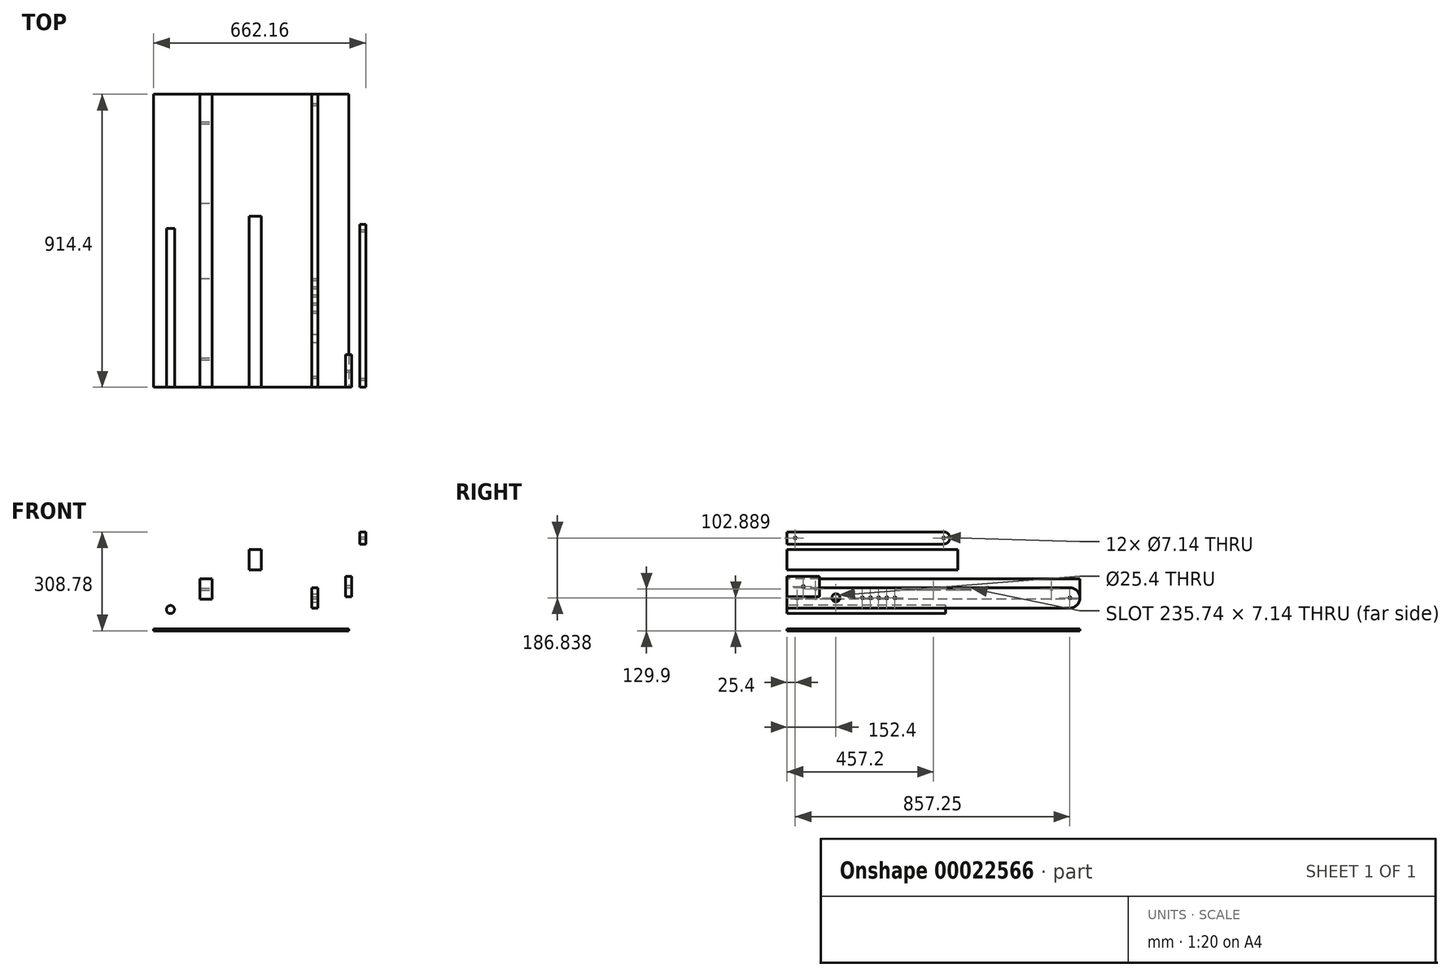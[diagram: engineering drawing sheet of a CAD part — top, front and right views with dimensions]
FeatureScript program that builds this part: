
annotation { "Feature Type Name" : "Feature", "Feature Type Description" : "" }
export const myFeature = defineFeature(function(context is Context, id is Id, definition is map)
    precondition{}
    {
        {
            var Q0;
            Q0=qCreatedBy(makeId("Front.planeOp"),FACE);
            var sketch = newSketch(context, id + "F0", { "sketchPlane" : qUnion([Q0])});
            skLineSegment(sketch, "E0.bottom", {"start": v(38.1, 63.5) * mm, "end": v(0, 63.5) * mm});
            skLineSegment(sketch, "E0.top", {"start": v(38.1, 0) * mm, "end": v(0, 0) * mm});
            skLineSegment(sketch, "E0.left", {"start": v(38.1, 63.5) * mm, "end": v(38.1, 0) * mm});
            skLineSegment(sketch, "E0.right", {"start": v(0, 63.5) * mm, "end": v(0, 0) * mm});
            skSolve(sketch);
        }
        {
            var Q0;
            Q0=qSketchRegion(id+"F0",true);
            extrude(context, id + "F1", {"entities" : qUnion([Q0]), "oppositeDirection" : true, "depth" : 914.4 * mm});
        }
        {
            var Q0;
            Q0=qCreatedBy(makeId("Front.planeOp"),FACE);
            var sketch = newSketch(context, id + "F2", { "sketchPlane" : qUnion([Q0])});
            skLineSegment(sketch, "E1.bottom", {"start": v(153.85, 91.9) * mm, "end": v(191.95, 91.9) * mm});
            skLineSegment(sketch, "E1.top", {"start": v(153.85, 155.4) * mm, "end": v(191.95, 155.4) * mm});
            skLineSegment(sketch, "E1.left", {"start": v(153.85, 91.9) * mm, "end": v(153.85, 155.4) * mm});
            skLineSegment(sketch, "E1.right", {"start": v(191.95, 91.9) * mm, "end": v(191.95, 155.4) * mm});
            skSolve(sketch);
        }
        {
            var Q0;
            Q0=makeQuery(id+"F2.imprint","IMPRINT",FACE,{"disambiguationData":[TD([[makeQuery(id+"F2.imprint","IMPRINT",EDGE,{"derivedFrom":sQuery(id+"F2.wireOp",EDGE,"E1.bottom")}),1.0]])]});
            extrude(context, id + "F3", {"entities" : qUnion([Q0]), "oppositeDirection" : true, "depth" : 533.4 * mm});
        }
        {
            var Q0;
            Q0=qCreatedBy(makeId("Front.planeOp"),FACE);
            var sketch = newSketch(context, id + "F4", { "sketchPlane" : qUnion([Q0])});
            skLineSegment(sketch, "E2.bottom", {"start": v(349.93, -27.01) * mm, "end": v(368.98, -27.01) * mm});
            skLineSegment(sketch, "E2.top", {"start": v(349.93, 36.49) * mm, "end": v(368.98, 36.49) * mm});
            skLineSegment(sketch, "E2.left", {"start": v(349.93, -27.01) * mm, "end": v(349.93, 36.49) * mm});
            skLineSegment(sketch, "E2.right", {"start": v(368.98, -27.01) * mm, "end": v(368.98, 36.49) * mm});
            skSolve(sketch);
        }
        {
            var Q0;
            Q0=qSketchRegion(id+"F4",true);
            extrude(context, id + "F5", {"entities" : qUnion([Q0]), "oppositeDirection" : true, "depth" : 914.4 * mm});
        }
        {
            var Q0;
            Q0=qCreatedBy(makeId("Front.planeOp"),FACE);
            var sketch = newSketch(context, id + "F6", { "sketchPlane" : qUnion([Q0])});
            skLineSegment(sketch, "E3.bottom", {"start": v(454.55, 8.02) * mm, "end": v(473.6, 8.02) * mm});
            skLineSegment(sketch, "E3.top", {"start": v(454.55, 71.52) * mm, "end": v(473.6, 71.52) * mm});
            skLineSegment(sketch, "E3.left", {"start": v(454.55, 8.02) * mm, "end": v(454.55, 71.52) * mm});
            skLineSegment(sketch, "E3.right", {"start": v(473.6, 8.02) * mm, "end": v(473.6, 71.52) * mm});
            skSolve(sketch);
        }
        {
            var Q0;
            Q0=qSketchRegion(id+"F6",true);
            extrude(context, id + "F7", {"entities" : qUnion([Q0]), "oppositeDirection" : true, "depth" : 101.6 * mm});
        }
        {
            var Q0;
            Q0=makeQuery(id+"F5.opExtrude","SWEPT_FACE",FACE,{"disambiguationData":[OSD([sQuery(id+"F4.wireOp",EDGE,"E2.right")])]});
            var sketch = newSketch(context, id + "F8", { "sketchPlane" : qUnion([Q0])});
            skArc(sketch, "E4", {"start": v(882.65, -27.01) * mm, "mid": v(914.4, 4.74) * mm, "end": v(882.65, 36.49) * mm});
            skLineSegment(sketch, "E5", {"start": v(882.65, 36.49) * mm, "end": v(914.4, 36.49) * mm});
            skLineSegment(sketch, "E6", {"start": v(914.4, 36.49) * mm, "end": v(914.4, -27.01) * mm});
            skLineSegment(sketch, "E7", {"start": v(914.4, -27.01) * mm, "end": v(882.65, -27.01) * mm});
            skSolve(sketch);
        }
        {
            var Q0;
            Q0=qSketchRegion(id+"F8",true);
            extrude(context, id + "F9", {"entities" : qUnion([Q0]), "operationType" : NewBodyOperationType.REMOVE, "endBound" : BoundingType.UP_TO_NEXT, "oppositeDirection" : true, "depth" : 25.4 * mm});
        }
        {
            var Q0;
            Q0=makeQuery(id+"F7.opExtrude","SWEPT_FACE",FACE,{"disambiguationData":[OSD([sQuery(id+"F6.wireOp",EDGE,"E3.right")])]});
            var sketch = newSketch(context, id + "F10", { "sketchPlane" : qUnion([Q0])});
            skLineSegment(sketch, "E8", {"start": v(50.8, 71.52) * mm, "end": v(50.8, 8.02) * mm, "construction": true});
            skCircle(sketch, "E9", {"center": v(50.8, 39.77) * mm, "radius": 3.57 * mm});
            skSolve(sketch);
        }
        {
            var Q0;
            Q0=qSketchRegion(id+"F10",true);
            extrude(context, id + "F11", {"entities" : qUnion([Q0]), "operationType" : NewBodyOperationType.REMOVE, "endBound" : BoundingType.UP_TO_NEXT, "oppositeDirection" : true, "depth" : 25.4 * mm});
        }
        {
            var Q0;
            Q0=makeQuery(id+"F5.opExtrude","SWEPT_FACE",FACE,{"disambiguationData":[OSD([sQuery(id+"F4.wireOp",EDGE,"E2.right")])]});
            var sketch = newSketch(context, id + "F12", { "sketchPlane" : qUnion([Q0])});
            skCircle(sketch, "E10", {"center": v(882.65, 4.74) * mm, "radius": 3.57 * mm});
            skSolve(sketch);
        }
        {
            var Q0;
            Q0=qSketchRegion(id+"F12",true);
            extrude(context, id + "F13", {"entities" : qUnion([Q0]), "operationType" : NewBodyOperationType.REMOVE, "endBound" : BoundingType.UP_TO_NEXT, "oppositeDirection" : true, "depth" : 25.4 * mm});
        }
        {
            var Q0;
            Q0=qCreatedBy(makeId("Front.planeOp"),FACE);
            var sketch = newSketch(context, id + "F14", { "sketchPlane" : qUnion([Q0])});
            skLineSegment(sketch, "E11.bottom", {"start": v(498.95, 172.53) * mm, "end": v(518, 172.53) * mm});
            skLineSegment(sketch, "E11.top", {"start": v(498.95, 210.63) * mm, "end": v(518, 210.63) * mm});
            skLineSegment(sketch, "E11.left", {"start": v(498.95, 172.53) * mm, "end": v(498.95, 210.63) * mm});
            skLineSegment(sketch, "E11.right", {"start": v(518, 172.53) * mm, "end": v(518, 210.63) * mm});
            skSolve(sketch);
        }
        {
            var Q0;
            Q0=qSketchRegion(id+"F14",true);
            extrude(context, id + "F15", {"entities" : qUnion([Q0]), "oppositeDirection" : true, "depth" : 508 * mm});
        }
        {
            var Q0;
            Q0=makeQuery(id+"F15.opExtrude","SWEPT_FACE",FACE,{"disambiguationData":[OSD([sQuery(id+"F14.wireOp",EDGE,"E11.right")])]});
            var sketch = newSketch(context, id + "F16", { "sketchPlane" : qUnion([Q0])});
            skArc(sketch, "E12", {"start": v(488.95, 172.53) * mm, "mid": v(508, 191.58) * mm, "end": v(488.95, 210.63) * mm});
            skLineSegment(sketch, "E13", {"start": v(488.95, 210.63) * mm, "end": v(508, 210.63) * mm});
            skLineSegment(sketch, "E14", {"start": v(508, 210.63) * mm, "end": v(508, 172.53) * mm});
            skLineSegment(sketch, "E15", {"start": v(508, 172.53) * mm, "end": v(488.95, 172.53) * mm});
            skSolve(sketch);
        }
        {
            var Q0;
            Q0=qSketchRegion(id+"F16",true);
            extrude(context, id + "F17", {"entities" : qUnion([Q0]), "operationType" : NewBodyOperationType.REMOVE, "endBound" : BoundingType.UP_TO_NEXT, "oppositeDirection" : true, "depth" : 25.4 * mm});
        }
        {
            var Q0;
            Q0=makeQuery(id+"F15.opExtrude","SWEPT_FACE",FACE,{"disambiguationData":[OSD([sQuery(id+"F14.wireOp",EDGE,"E11.right")])]});
            var sketch = newSketch(context, id + "F18", { "sketchPlane" : qUnion([Q0])});
            skCircle(sketch, "E16", {"center": v(488.95, 191.58) * mm, "radius": 3.57 * mm});
            skSolve(sketch);
        }
        {
            var Q0;
            Q0=qSketchRegion(id+"F18",true);
            extrude(context, id + "F19", {"entities" : qUnion([Q0]), "operationType" : NewBodyOperationType.REMOVE, "endBound" : BoundingType.UP_TO_NEXT, "oppositeDirection" : true, "depth" : 25.4 * mm});
        }
        {
            var Q0;
            Q0=makeQuery(id+"F1.opExtrude","SWEPT_FACE",FACE,{"disambiguationData":[OSD([sQuery(id+"F0.wireOp",EDGE,"E0.left")])]});
            var sketch = newSketch(context, id + "F20", { "sketchPlane" : qUnion([Q0])});
            skLineSegment(sketch, "E17", {"start": v(914.4, 31.75) * mm, "end": v(0, 31.75) * mm, "construction": true});
            skArc(sketch, "E18", {"start": v(342.9, 35.32) * mm, "mid": v(339.33, 31.75) * mm, "end": v(342.9, 28.18) * mm});
            skLineSegment(sketch, "E19.direction1", {"start": v(342.9, 31.75) * mm, "end": v(571.5, 31.75) * mm, "construction": true});
            skArc(sketch, "E20", {"start": v(571.5, 28.18) * mm, "mid": v(575.07, 31.75) * mm, "end": v(571.5, 35.32) * mm});
            skLineSegment(sketch, "E21", {"start": v(342.9, 35.32) * mm, "end": v(571.5, 35.32) * mm});
            skLineSegment(sketch, "E22", {"start": v(571.5, 28.18) * mm, "end": v(342.9, 28.18) * mm});
            skCircle(sketch, "E23", {"center": v(825.5, 31.75) * mm, "radius": 3.57 * mm});
            skLineSegment(sketch, "E24", {"start": v(457.2, 0) * mm, "end": v(457.2, 63.5) * mm, "construction": true});
            skCircle(sketch, "E25.MirrorC", {"center": v(88.9, 31.75) * mm, "radius": 3.57 * mm});
            skCircle(sketch, "E26.MirrorC", {"center": v(88.9, 31.75) * mm, "radius": 3.57 * mm, "construction": true});
            skSolve(sketch);
        }
        {
            var Q0;
            Q0=qSketchRegion(id+"F20",true);
            extrude(context, id + "F21", {"entities" : qUnion([Q0]), "operationType" : NewBodyOperationType.REMOVE, "endBound" : BoundingType.UP_TO_NEXT, "oppositeDirection" : true, "depth" : 25.4 * mm});
        }
        {
            var Q0;
            Q0=makeQuery(id+"F5.opExtrude","SWEPT_FACE",FACE,{"disambiguationData":[OSD([sQuery(id+"F4.wireOp",EDGE,"E2.right")])]});
            var sketch = newSketch(context, id + "F22", { "sketchPlane" : qUnion([Q0])});
            skLineSegment(sketch, "E27", {"start": v(0, 4.74) * mm, "end": v(914.4, 4.74) * mm, "construction": true});
            skCircle(sketch, "E28", {"center": v(31.75, 4.74) * mm, "radius": 3.57 * mm});
            skCircle(sketch, "E29", {"center": v(285.75, 4.74) * mm, "radius": 3.57 * mm});
            skCircle(sketch, "E30", {"center": v(260.35, 4.74) * mm, "radius": 3.57 * mm});
            skCircle(sketch, "E31", {"center": v(311.15, 4.74) * mm, "radius": 3.57 * mm});
            skCircle(sketch, "E32", {"center": v(336.55, 4.74) * mm, "radius": 3.57 * mm});
            skCircle(sketch, "E33", {"center": v(234.95, 4.74) * mm, "radius": 3.57 * mm});
            skSolve(sketch);
        }
        {
            var Q0;
            Q0=qSketchRegion(id+"F22",true);
            extrude(context, id + "F23", {"entities" : qUnion([Q0]), "operationType" : NewBodyOperationType.REMOVE, "endBound" : BoundingType.UP_TO_NEXT, "oppositeDirection" : true, "depth" : 25.4 * mm});
        }
        {
            var Q0;
            Q0=makeQuery(id+"F15.opExtrude","SWEPT_FACE",FACE,{"disambiguationData":[OSD([sQuery(id+"F14.wireOp",EDGE,"E11.right")])]});
            var sketch = newSketch(context, id + "F24", { "sketchPlane" : qUnion([Q0])});
            skLineSegment(sketch, "E34", {"start": v(0, 191.58) * mm, "end": v(25.4, 191.58) * mm, "construction": true});
            skCircle(sketch, "E35", {"center": v(25.4, 191.58) * mm, "radius": 3.57 * mm});
            skSolve(sketch);
        }
        {
            var Q0;
            Q0=qSketchRegion(id+"F24",true);
            extrude(context, id + "F25", {"entities" : qUnion([Q0]), "operationType" : NewBodyOperationType.REMOVE, "endBound" : BoundingType.UP_TO_NEXT, "oppositeDirection" : true, "depth" : 25.4 * mm});
        }
        {
            var Q0;
            Q0=qCreatedBy(makeId("Front.planeOp"),FACE);
            var sketch = newSketch(context, id + "F33", { "sketchPlane" : qUnion([Q0])});
            skCircle(sketch, "E36", {"center": v(-91.76, -31.76) * mm, "radius": 12.7 * mm});
            skSolve(sketch);
        }
        {
            var Q0;
            Q0=makeQuery(id+"F33.imprint","IMPRINT",FACE,{"disambiguationData":[TD([[makeQuery(id+"F33.imprint","IMPRINT",EDGE,{"derivedFrom":sQuery(id+"F33.wireOp",EDGE,"E36")}),1.0]])]});
            extrude(context, id + "F26", {"entities" : qUnion([Q0]), "oppositeDirection" : true, "depth" : 495.3 * mm});
        }
        {
            var Q0;
            Q0=qCreatedBy(makeId("Front.planeOp"),FACE);
            var sketch = newSketch(context, id + "F27", { "sketchPlane" : qUnion([Q0])});
            skLineSegment(sketch, "E37.bottom", {"start": v(-144.16, -91.8) * mm, "end": v(465.44, -91.8) * mm});
            skLineSegment(sketch, "E37.top", {"start": v(-144.16, -98.15) * mm, "end": v(465.44, -98.15) * mm});
            skLineSegment(sketch, "E37.left", {"start": v(-144.16, -91.8) * mm, "end": v(-144.16, -98.15) * mm});
            skLineSegment(sketch, "E37.right", {"start": v(465.44, -91.8) * mm, "end": v(465.44, -98.15) * mm});
            skSolve(sketch);
        }
        {
            var Q0;
            Q0=qSketchRegion(id+"F27",true);
            extrude(context, id + "F28", {"entities" : qUnion([Q0]), "oppositeDirection" : true, "depth" : 914.4 * mm});
        }
        {
            var Q0;
            Q0=makeQuery(id+"F5.opExtrude","SWEPT_FACE",FACE,{"disambiguationData":[OSD([sQuery(id+"F4.wireOp",EDGE,"E2.right")])]});
            var sketch = newSketch(context, id + "F29", { "sketchPlane" : qUnion([Q0])});
            skLineSegment(sketch, "E38", {"start": v(0, 4.74) * mm, "end": v(914.4, 4.74) * mm, "construction": true});
            skCircle(sketch, "E39", {"center": v(152.4, 4.74) * mm, "radius": 12.7 * mm});
            skSolve(sketch);
        }
        {
            var Q0;
            Q0=qSketchRegion(id+"F29",true);
            extrude(context, id + "F30", {"entities" : qUnion([Q0]), "operationType" : NewBodyOperationType.REMOVE, "endBound" : BoundingType.UP_TO_NEXT, "oppositeDirection" : true, "depth" : 25.4 * mm});
        }
        {
            var Q0;
            Q0=makeQuery(id+"F1.opExtrude","SWEPT_FACE",FACE,{"disambiguationData":[OSD([sQuery(id+"F0.wireOp",EDGE,"E0.right")])]});
            var sketch = newSketch(context, id + "F31", { "sketchPlane" : qUnion([Q0])});
            skLineSegment(sketch, "E40", {"start": v(-571.5, 31.75) * mm, "end": v(-342.9, 31.75) * mm});
            skSolve(sketch);
        }
        {
            var Q0;
            Q0=makeQuery(id+"F1.opExtrude","SWEPT_FACE",FACE,{"disambiguationData":[OSD([sQuery(id+"F0.wireOp",EDGE,"E0.left")])]});
            var sketch = newSketch(context, id + "F32", { "sketchPlane" : qUnion([Q0])});
            skLineSegment(sketch, "E41", {"start": v(342.9, 31.75) * mm, "end": v(571.5, 31.75) * mm});
            skSolve(sketch);
        }
    });
